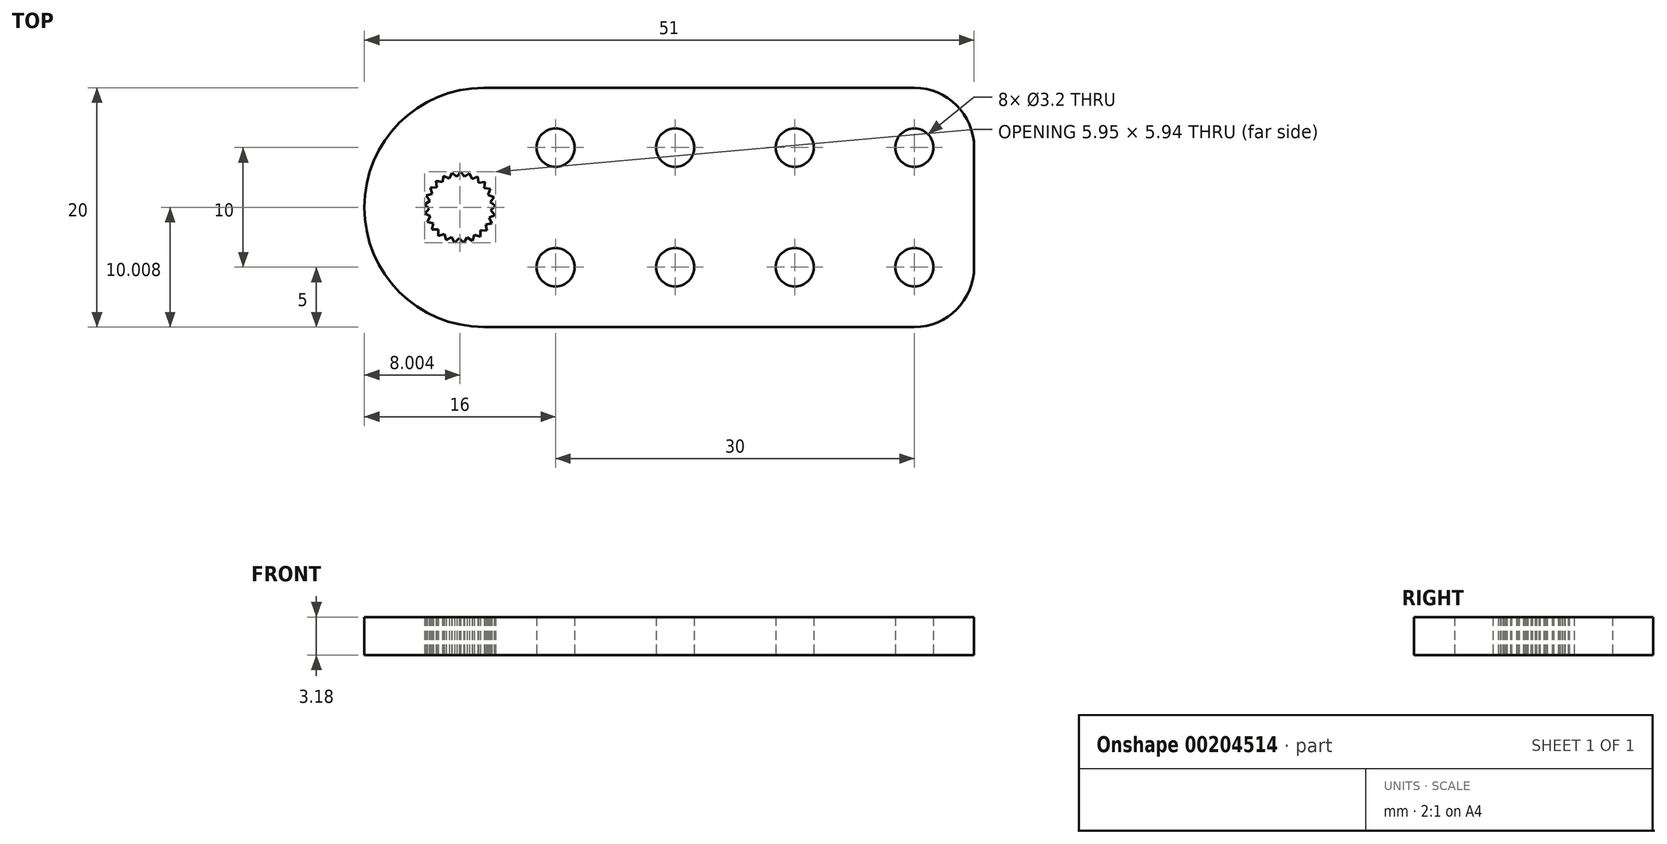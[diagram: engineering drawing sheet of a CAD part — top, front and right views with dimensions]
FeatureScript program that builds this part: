
annotation { "Feature Type Name" : "Feature", "Feature Type Description" : "" }
export const myFeature = defineFeature(function(context is Context, id is Id, definition is map)
    precondition{}
    {
        {
            var Q0;
            Q0=qCreatedBy(makeId("Top.planeOp"),FACE);
            var sketch = newSketch(context, id + "F0", { "sketchPlane" : qUnion([Q0])});
            skLineSegment(sketch, "E0.bottom", {"start": v(10, 0) * mm, "end": v(46, 0) * mm});
            skLineSegment(sketch, "E0.top", {"start": v(10, 20) * mm, "end": v(46, 20) * mm});
            skLineSegment(sketch, "E0.right", {"start": v(51, 5) * mm, "end": v(51, 15) * mm});
            skCircle(sketch, "E1", {"center": v(46, 15) * mm, "radius": 1.6 * mm});
            skCircle(sketch, "E2.0.1.0", {"center": v(46, 5) * mm, "radius": 1.6 * mm});
            skCircle(sketch, "E2.1.0.0", {"center": v(36, 15) * mm, "radius": 1.6 * mm});
            skCircle(sketch, "E2.1.1.0", {"center": v(36, 5) * mm, "radius": 1.6 * mm});
            skCircle(sketch, "E2.2.0.0", {"center": v(26, 15) * mm, "radius": 1.6 * mm});
            skCircle(sketch, "E2.2.1.0", {"center": v(26, 5) * mm, "radius": 1.6 * mm});
            skCircle(sketch, "E2.3.0.0", {"center": v(16, 15) * mm, "radius": 1.6 * mm});
            skCircle(sketch, "E2.3.1.0", {"center": v(16, 5) * mm, "radius": 1.6 * mm});
            skLineSegment(sketch, "E2.direction1", {"start": v(46, 15) * mm, "end": v(36, 15) * mm, "construction": true});
            skLineSegment(sketch, "E2.direction2", {"start": v(46, 15) * mm, "end": v(46, 5) * mm, "construction": true});
            skLineSegment(sketch, "E3", {"start": v(5.52, 11.65) * mm, "end": v(5.69, 11.15) * mm});
            skLineSegment(sketch, "E4", {"start": v(5.69, 11.15) * mm, "end": v(5.19, 10.98) * mm});
            skLineSegment(sketch, "E5.1.0", {"start": v(5.19, 10.98) * mm, "end": v(5.47, 10.54) * mm});
            skLineSegment(sketch, "E5.1.1", {"start": v(5.47, 10.54) * mm, "end": v(5.03, 10.25) * mm});
            skLineSegment(sketch, "E5.2.0", {"start": v(5.03, 10.25) * mm, "end": v(5.42, 9.9) * mm});
            skLineSegment(sketch, "E5.2.1", {"start": v(5.42, 9.9) * mm, "end": v(5.06, 9.5) * mm});
            skLineSegment(sketch, "E5.3.0", {"start": v(5.06, 9.5) * mm, "end": v(5.53, 9.26) * mm});
            skLineSegment(sketch, "E5.3.1", {"start": v(5.53, 9.26) * mm, "end": v(5.28, 8.8) * mm});
            skLineSegment(sketch, "E5.4.0", {"start": v(5.28, 8.8) * mm, "end": v(5.79, 8.66) * mm});
            skLineSegment(sketch, "E5.4.1", {"start": v(5.79, 8.66) * mm, "end": v(5.66, 8.15) * mm});
            skLineSegment(sketch, "E5.5.0", {"start": v(5.66, 8.15) * mm, "end": v(6.2, 8.16) * mm});
            skLineSegment(sketch, "E5.5.1", {"start": v(6.2, 8.16) * mm, "end": v(6.2, 7.63) * mm});
            skLineSegment(sketch, "E5.6.0", {"start": v(6.2, 7.63) * mm, "end": v(6.7, 7.76) * mm});
            skLineSegment(sketch, "E5.6.1", {"start": v(6.7, 7.76) * mm, "end": v(6.84, 7.25) * mm});
            skLineSegment(sketch, "E5.7.0", {"start": v(6.84, 7.25) * mm, "end": v(7.3, 7.51) * mm});
            skLineSegment(sketch, "E5.7.1", {"start": v(7.3, 7.51) * mm, "end": v(7.56, 7.05) * mm});
            skLineSegment(sketch, "E5.8.0", {"start": v(7.56, 7.05) * mm, "end": v(7.94, 7.42) * mm});
            skLineSegment(sketch, "E5.8.1", {"start": v(7.94, 7.42) * mm, "end": v(8.3, 7.04) * mm});
            skLineSegment(sketch, "E5.9.0", {"start": v(8.3, 7.04) * mm, "end": v(8.59, 7.48) * mm});
            skLineSegment(sketch, "E5.9.1", {"start": v(8.59, 7.48) * mm, "end": v(9.04, 7.2) * mm});
            skLineSegment(sketch, "E5.10.0", {"start": v(9.04, 7.2) * mm, "end": v(9.2, 7.7) * mm});
            skLineSegment(sketch, "E5.10.1", {"start": v(9.2, 7.7) * mm, "end": v(9.7, 7.55) * mm});
            skLineSegment(sketch, "E5.11.0", {"start": v(9.7, 7.55) * mm, "end": v(9.73, 8.08) * mm});
            skLineSegment(sketch, "E5.11.1", {"start": v(9.73, 8.08) * mm, "end": v(10.25, 8.05) * mm});
            skLineSegment(sketch, "E5.12.0", {"start": v(10.25, 8.05) * mm, "end": v(10.15, 8.57) * mm});
            skLineSegment(sketch, "E5.12.1", {"start": v(10.15, 8.57) * mm, "end": v(10.67, 8.67) * mm});
            skLineSegment(sketch, "E5.13.0", {"start": v(10.67, 8.67) * mm, "end": v(10.44, 9.15) * mm});
            skLineSegment(sketch, "E5.13.1", {"start": v(10.44, 9.15) * mm, "end": v(10.91, 9.38) * mm});
            skLineSegment(sketch, "E5.14.0", {"start": v(10.91, 9.38) * mm, "end": v(10.57, 9.78) * mm});
            skLineSegment(sketch, "E5.14.1", {"start": v(10.57, 9.78) * mm, "end": v(10.98, 10.12) * mm});
            skLineSegment(sketch, "E5.15.0", {"start": v(10.98, 10.12) * mm, "end": v(10.55, 10.43) * mm});
            skLineSegment(sketch, "E5.15.1", {"start": v(10.55, 10.43) * mm, "end": v(10.85, 10.86) * mm});
            skLineSegment(sketch, "E5.16.0", {"start": v(10.85, 10.86) * mm, "end": v(10.36, 11.05) * mm});
            skLineSegment(sketch, "E5.16.1", {"start": v(10.36, 11.05) * mm, "end": v(10.55, 11.54) * mm});
            skLineSegment(sketch, "E5.17.0", {"start": v(10.55, 11.54) * mm, "end": v(10.03, 11.6) * mm});
            skLineSegment(sketch, "E5.17.1", {"start": v(10.03, 11.6) * mm, "end": v(10.09, 12.13) * mm});
            skLineSegment(sketch, "E5.18.0", {"start": v(10.09, 12.13) * mm, "end": v(9.56, 12.06) * mm});
            skLineSegment(sketch, "E5.18.1", {"start": v(9.56, 12.06) * mm, "end": v(9.5, 12.58) * mm});
            skLineSegment(sketch, "E5.19.0", {"start": v(9.5, 12.58) * mm, "end": v(9, 12.38) * mm});
            skLineSegment(sketch, "E5.19.1", {"start": v(9, 12.38) * mm, "end": v(8.8, 12.87) * mm});
            skLineSegment(sketch, "E5.20.0", {"start": v(8.8, 12.87) * mm, "end": v(8.38, 12.56) * mm});
            skLineSegment(sketch, "E5.20.1", {"start": v(8.38, 12.56) * mm, "end": v(8.07, 12.98) * mm});
            skLineSegment(sketch, "E5.21.0", {"start": v(8.07, 12.98) * mm, "end": v(7.73, 12.57) * mm});
            skLineSegment(sketch, "E5.21.1", {"start": v(7.73, 12.57) * mm, "end": v(7.32, 12.9) * mm});
            skLineSegment(sketch, "E5.22.0", {"start": v(7.32, 12.9) * mm, "end": v(7.1, 12.42) * mm});
            skLineSegment(sketch, "E5.22.1", {"start": v(7.1, 12.42) * mm, "end": v(6.62, 12.64) * mm});
            skLineSegment(sketch, "E5.23.0", {"start": v(6.62, 12.64) * mm, "end": v(6.53, 12.12) * mm});
            skLineSegment(sketch, "E5.23.1", {"start": v(6.53, 12.12) * mm, "end": v(6, 12.22) * mm});
            skLineSegment(sketch, "E5.24.0", {"start": v(6, 12.22) * mm, "end": v(6.05, 11.69) * mm});
            skLineSegment(sketch, "E5.24.1", {"start": v(6.05, 11.69) * mm, "end": v(5.52, 11.65) * mm});
            skPoint(sketch, "E5.center", {"position": v(8, 10) * mm});
            skArc(sketch, "E6", {"start": v(10, 20) * mm, "mid": v(2.93, 17.07) * mm, "end": v(0, 10) * mm});
            skPoint(sketch, "E7.orphan", {"position": v(0, 20) * mm});
            skArc(sketch, "E8.MirrorCS", {"start": v(10, 0) * mm, "mid": v(2.93, 2.93) * mm, "end": v(0, 10) * mm});
            skPoint(sketch, "E9.orphan", {"position": v(0, 0) * mm});
            skArc(sketch, "E10", {"start": v(51, 15) * mm, "mid": v(49.54, 18.54) * mm, "end": v(46, 20) * mm});
            skArc(sketch, "E11.MirrorCS", {"start": v(51, 5) * mm, "mid": v(49.54, 1.46) * mm, "end": v(46, 0) * mm});
            skSolve(sketch);
        }
        {
            var Q0;
            Q0 = qSketchRegion(id + "F0", true);
            extrude(context, id + "F1", {"entities" : qUnion([Q0]), "depth" : 3.17 * mm});
        }
    });
